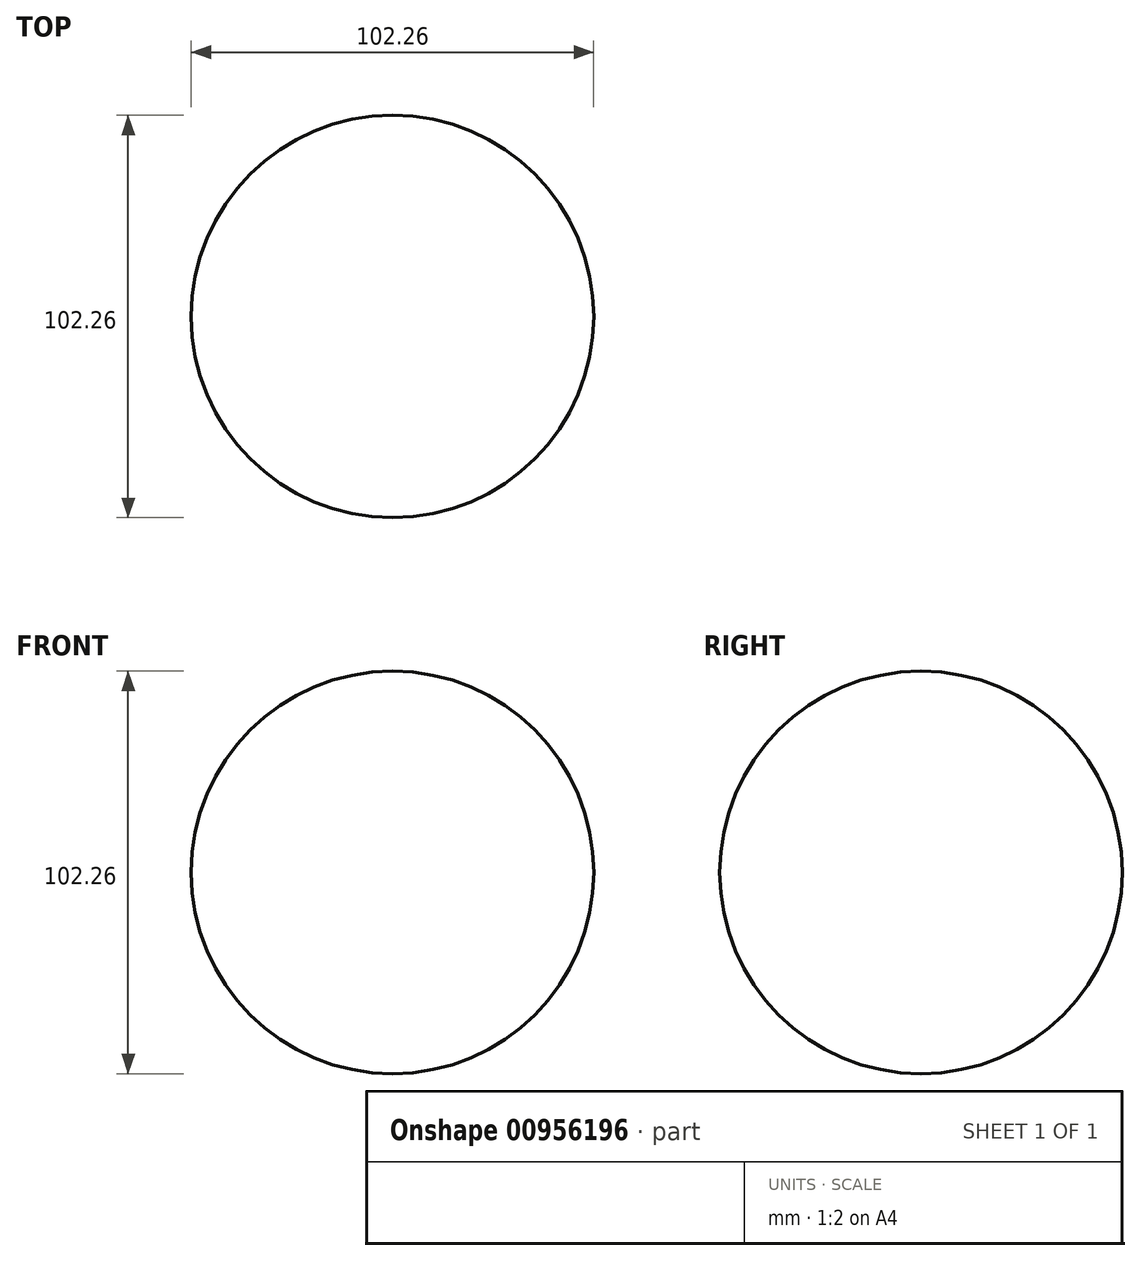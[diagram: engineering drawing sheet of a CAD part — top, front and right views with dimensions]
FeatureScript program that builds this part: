
annotation { "Feature Type Name" : "Feature", "Feature Type Description" : "" }
export const myFeature = defineFeature(function(context is Context, id is Id, definition is map)
    precondition{}
    {
        {
            var Q0;
            Q0=qCreatedBy(makeId("Front.planeOp"),FACE);
            var sketch = newSketch(context, id + "F0", { "sketchPlane" : qUnion([Q0])});
            skArc(sketch, "E0", {"start": v(0, 51.13) * mm, "mid": v(-51.13, 0) * mm, "end": v(0, -51.13) * mm});
            skLineSegment(sketch, "E1", {"start": v(0, 51.13) * mm, "end": v(0, -51.13) * mm});
            skSolve(sketch);
        }
        {
            var Q0;
            Q0=makeQuery(id+"F0.imprint","IMPRINT",FACE,{"disambiguationData":[TD([[makeQuery(id+"F0.imprint","IMPRINT",EDGE,{"derivedFrom":sQuery(id+"F0.wireOp",EDGE,"E0")}),1.0]])]});
            var Q1;
            Q1=sQuery(id+"F0.wireOp",EDGE,"E1");
            revolve(context, id + "F1", {"surfaceOperationType" : NewSurfaceOperationType.NEW, "entities" : qUnion([Q0]), "axis" : qUnion([Q1]), "revolveType" : RevolveType.FULL});
        }
    });
